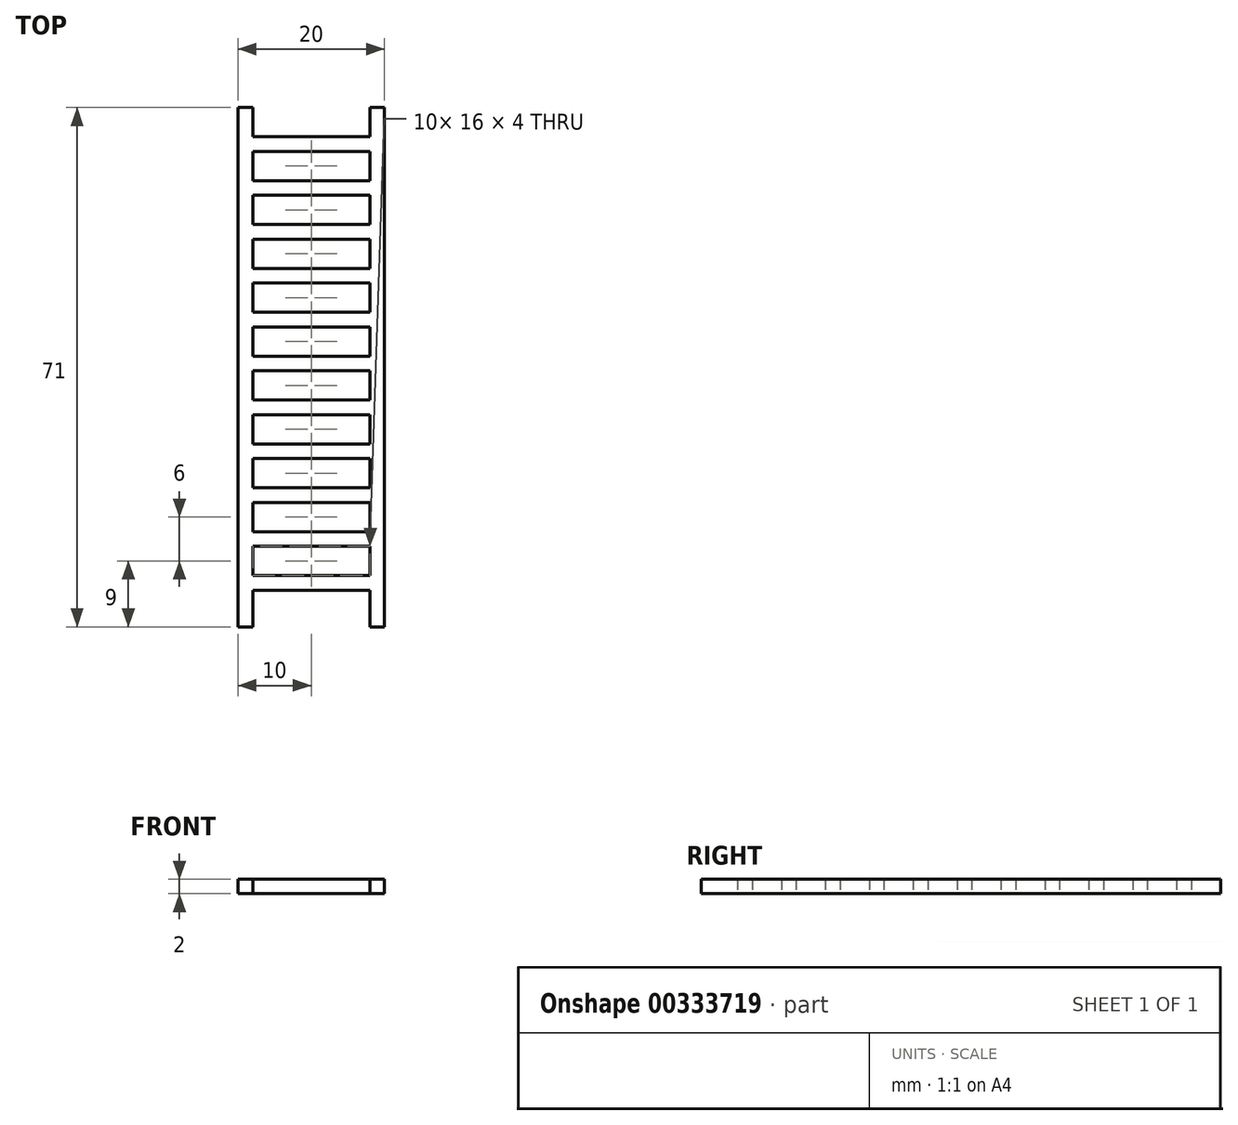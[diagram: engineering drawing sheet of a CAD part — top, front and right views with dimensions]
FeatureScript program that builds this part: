
annotation { "Feature Type Name" : "Feature", "Feature Type Description" : "" }
export const myFeature = defineFeature(function(context is Context, id is Id, definition is map)
    precondition{}
    {
        {
            var Q0;
            Q0=qCreatedBy(makeId("Top.planeOp"),FACE);
            var sketch = newSketch(context, id + "F0", { "sketchPlane" : qUnion([Q0])});
            skLineSegment(sketch, "E0.bottom", {"start": v(-10, 35.5) * mm, "end": v(10, 35.5) * mm, "construction": true});
            skLineSegment(sketch, "E0.top", {"start": v(-10, -35.5) * mm, "end": v(10, -35.5) * mm, "construction": true});
            skLineSegment(sketch, "E0.left", {"start": v(-10, 35.5) * mm, "end": v(-10, -35.5) * mm, "construction": true});
            skLineSegment(sketch, "E0.right", {"start": v(10, 35.5) * mm, "end": v(10, -35.5) * mm, "construction": true});
            skLineSegment(sketch, "E1", {"start": v(-10, 0) * mm, "end": v(10, 0) * mm, "construction": true});
            skLineSegment(sketch, "E2", {"start": v(0, 35.5) * mm, "end": v(0, -35.5) * mm, "construction": true});
            skLineSegment(sketch, "E3.bottom", {"start": v(-10, 35.5) * mm, "end": v(-8, 35.5) * mm});
            skLineSegment(sketch, "E3.top", {"start": v(-10, -35.5) * mm, "end": v(-8, -35.5) * mm});
            skLineSegment(sketch, "E3.left", {"start": v(-10, 35.5) * mm, "end": v(-10, -35.5) * mm});
            skLineSegment(sketch, "E3.right", {"start": v(-8, 35.5) * mm, "end": v(-8, -35.5) * mm});
            skLineSegment(sketch, "E4.bottom", {"start": v(10, -35.5) * mm, "end": v(8, -35.5) * mm});
            skLineSegment(sketch, "E4.top", {"start": v(10, 35.5) * mm, "end": v(8, 35.5) * mm});
            skLineSegment(sketch, "E4.left", {"start": v(10, -35.5) * mm, "end": v(10, 35.5) * mm});
            skLineSegment(sketch, "E4.right", {"start": v(8, -35.5) * mm, "end": v(8, 35.5) * mm});
            skLineSegment(sketch, "E5.bottom", {"start": v(-8, -28.5) * mm, "end": v(8, -28.5) * mm});
            skLineSegment(sketch, "E5.top", {"start": v(-8, -30.5) * mm, "end": v(8, -30.5) * mm});
            skLineSegment(sketch, "E5.left", {"start": v(-8, -28.5) * mm, "end": v(-8, -30.5) * mm});
            skLineSegment(sketch, "E5.right", {"start": v(8, -28.5) * mm, "end": v(8, -30.5) * mm});
            skLineSegment(sketch, "E6", {"start": v(-8, -29.5) * mm, "end": v(8, -29.5) * mm, "construction": true});
            skLineSegment(sketch, "E7.0.1.0", {"start": v(-8, -22.5) * mm, "end": v(8, -22.5) * mm});
            skLineSegment(sketch, "E7.0.1.1", {"start": v(-8, -24.5) * mm, "end": v(8, -24.5) * mm});
            skLineSegment(sketch, "E7.0.1.2", {"start": v(8, -22.5) * mm, "end": v(8, -24.5) * mm});
            skLineSegment(sketch, "E7.0.1.3", {"start": v(-8, -23.5) * mm, "end": v(8, -23.5) * mm, "construction": true});
            skLineSegment(sketch, "E7.0.1.4", {"start": v(-8, -22.5) * mm, "end": v(-8, -24.5) * mm});
            skLineSegment(sketch, "E7.0.2.0", {"start": v(-8, -16.5) * mm, "end": v(8, -16.5) * mm});
            skLineSegment(sketch, "E7.0.2.1", {"start": v(-8, -18.5) * mm, "end": v(8, -18.5) * mm});
            skLineSegment(sketch, "E7.0.2.2", {"start": v(8, -16.5) * mm, "end": v(8, -18.5) * mm});
            skLineSegment(sketch, "E7.0.2.3", {"start": v(-8, -17.5) * mm, "end": v(8, -17.5) * mm, "construction": true});
            skLineSegment(sketch, "E7.0.2.4", {"start": v(-8, -16.5) * mm, "end": v(-8, -18.5) * mm});
            skLineSegment(sketch, "E7.0.3.0", {"start": v(-8, -10.5) * mm, "end": v(8, -10.5) * mm});
            skLineSegment(sketch, "E7.0.3.1", {"start": v(-8, -12.5) * mm, "end": v(8, -12.5) * mm});
            skLineSegment(sketch, "E7.0.3.2", {"start": v(8, -10.5) * mm, "end": v(8, -12.5) * mm});
            skLineSegment(sketch, "E7.0.3.3", {"start": v(-8, -11.5) * mm, "end": v(8, -11.5) * mm, "construction": true});
            skLineSegment(sketch, "E7.0.3.4", {"start": v(-8, -10.5) * mm, "end": v(-8, -12.5) * mm});
            skLineSegment(sketch, "E7.0.4.0", {"start": v(-8, -4.5) * mm, "end": v(8, -4.5) * mm});
            skLineSegment(sketch, "E7.0.4.1", {"start": v(-8, -6.5) * mm, "end": v(8, -6.5) * mm});
            skLineSegment(sketch, "E7.0.4.2", {"start": v(8, -4.5) * mm, "end": v(8, -6.5) * mm});
            skLineSegment(sketch, "E7.0.4.3", {"start": v(-8, -5.5) * mm, "end": v(8, -5.5) * mm, "construction": true});
            skLineSegment(sketch, "E7.0.4.4", {"start": v(-8, -4.5) * mm, "end": v(-8, -6.5) * mm});
            skLineSegment(sketch, "E7.0.5.0", {"start": v(-8, 1.5) * mm, "end": v(8, 1.5) * mm});
            skLineSegment(sketch, "E7.0.5.1", {"start": v(-8, -0.5) * mm, "end": v(8, -0.5) * mm});
            skLineSegment(sketch, "E7.0.5.2", {"start": v(8, 1.5) * mm, "end": v(8, -0.5) * mm});
            skLineSegment(sketch, "E7.0.5.3", {"start": v(-8, 0.5) * mm, "end": v(8, 0.5) * mm, "construction": true});
            skLineSegment(sketch, "E7.0.5.4", {"start": v(-8, 1.5) * mm, "end": v(-8, -0.5) * mm});
            skLineSegment(sketch, "E7.0.6.0", {"start": v(-8, 7.5) * mm, "end": v(8, 7.5) * mm});
            skLineSegment(sketch, "E7.0.6.1", {"start": v(-8, 5.5) * mm, "end": v(8, 5.5) * mm});
            skLineSegment(sketch, "E7.0.6.2", {"start": v(8, 7.5) * mm, "end": v(8, 5.5) * mm});
            skLineSegment(sketch, "E7.0.6.3", {"start": v(-8, 6.5) * mm, "end": v(8, 6.5) * mm, "construction": true});
            skLineSegment(sketch, "E7.0.6.4", {"start": v(-8, 7.5) * mm, "end": v(-8, 5.5) * mm});
            skLineSegment(sketch, "E7.0.7.0", {"start": v(-8, 13.5) * mm, "end": v(8, 13.5) * mm});
            skLineSegment(sketch, "E7.0.7.1", {"start": v(-8, 11.5) * mm, "end": v(8, 11.5) * mm});
            skLineSegment(sketch, "E7.0.7.2", {"start": v(8, 13.5) * mm, "end": v(8, 11.5) * mm});
            skLineSegment(sketch, "E7.0.7.3", {"start": v(-8, 12.5) * mm, "end": v(8, 12.5) * mm, "construction": true});
            skLineSegment(sketch, "E7.0.7.4", {"start": v(-8, 13.5) * mm, "end": v(-8, 11.5) * mm});
            skLineSegment(sketch, "E7.0.8.0", {"start": v(-8, 19.5) * mm, "end": v(8, 19.5) * mm});
            skLineSegment(sketch, "E7.0.8.1", {"start": v(-8, 17.5) * mm, "end": v(8, 17.5) * mm});
            skLineSegment(sketch, "E7.0.8.2", {"start": v(8, 19.5) * mm, "end": v(8, 17.5) * mm});
            skLineSegment(sketch, "E7.0.8.3", {"start": v(-8, 18.5) * mm, "end": v(8, 18.5) * mm, "construction": true});
            skLineSegment(sketch, "E7.0.8.4", {"start": v(-8, 19.5) * mm, "end": v(-8, 17.5) * mm});
            skLineSegment(sketch, "E7.0.9.0", {"start": v(-8, 25.5) * mm, "end": v(8, 25.5) * mm});
            skLineSegment(sketch, "E7.0.9.1", {"start": v(-8, 23.5) * mm, "end": v(8, 23.5) * mm});
            skLineSegment(sketch, "E7.0.9.2", {"start": v(8, 25.5) * mm, "end": v(8, 23.5) * mm});
            skLineSegment(sketch, "E7.0.9.3", {"start": v(-8, 24.5) * mm, "end": v(8, 24.5) * mm, "construction": true});
            skLineSegment(sketch, "E7.0.9.4", {"start": v(-8, 25.5) * mm, "end": v(-8, 23.5) * mm});
            skLineSegment(sketch, "E7.0.10.0", {"start": v(-8, 31.5) * mm, "end": v(8, 31.5) * mm});
            skLineSegment(sketch, "E7.0.10.1", {"start": v(-8, 29.5) * mm, "end": v(8, 29.5) * mm});
            skLineSegment(sketch, "E7.0.10.2", {"start": v(8, 31.5) * mm, "end": v(8, 29.5) * mm});
            skLineSegment(sketch, "E7.0.10.3", {"start": v(-8, 30.5) * mm, "end": v(8, 30.5) * mm, "construction": true});
            skLineSegment(sketch, "E7.0.10.4", {"start": v(-8, 31.5) * mm, "end": v(-8, 29.5) * mm});
            skLineSegment(sketch, "E7.direction1", {"start": v(-8, -30.5) * mm, "end": v(17, -30.5) * mm, "construction": true});
            skLineSegment(sketch, "E7.direction2", {"start": v(-8, -30.5) * mm, "end": v(-8, -24.5) * mm, "construction": true});
            skSolve(sketch);
        }
        {
            var Q0;
            {var subQ11=sQuery(id+"F0.wireOp",EDGE,"E4.bottom");Q0=makeQuery(id+"F0.imprint","IMPRINT",FACE,{"disambiguationData":[TD([[makeQuery(id+"F0.imprint","IMPRINT",EDGE,{"derivedFrom":subQ11}),-1.0]])]});}
            var Q1;
            Q1=makeQuery(id+"F0.imprint","IMPRINT",FACE,{"disambiguationData":[TD([[makeQuery(id+"F0.imprint","IMPRINT",EDGE,{"derivedFrom":sQuery(id+"F0.wireOp",EDGE,"E5.bottom")}),-1.0]])]});
            var Q2;
            Q2=makeQuery(id+"F0.imprint","IMPRINT",FACE,{"disambiguationData":[TD([[makeQuery(id+"F0.imprint","IMPRINT",EDGE,{"derivedFrom":sQuery(id+"F0.wireOp",EDGE,"E7.0.1.0")}),-1.0]])]});
            var Q3;
            {var subQ9=sQuery(id+"F0.wireOp",EDGE,"E3.bottom");Q3=makeQuery(id+"F0.imprint","IMPRINT",FACE,{"disambiguationData":[TD([[makeQuery(id+"F0.imprint","IMPRINT",EDGE,{"derivedFrom":subQ9}),-1.0]])]});}
            var Q4;
            Q4=makeQuery(id+"F0.imprint","IMPRINT",FACE,{"disambiguationData":[TD([[makeQuery(id+"F0.imprint","IMPRINT",EDGE,{"derivedFrom":sQuery(id+"F0.wireOp",EDGE,"E7.0.2.0")}),-1.0]])]});
            var Q5;
            Q5=makeQuery(id+"F0.imprint","IMPRINT",FACE,{"disambiguationData":[TD([[makeQuery(id+"F0.imprint","IMPRINT",EDGE,{"derivedFrom":sQuery(id+"F0.wireOp",EDGE,"E7.0.3.0")}),-1.0]])]});
            var Q6;
            Q6=makeQuery(id+"F0.imprint","IMPRINT",FACE,{"disambiguationData":[TD([[makeQuery(id+"F0.imprint","IMPRINT",EDGE,{"derivedFrom":sQuery(id+"F0.wireOp",EDGE,"E7.0.4.0")}),-1.0]])]});
            var Q7;
            Q7=makeQuery(id+"F0.imprint","IMPRINT",FACE,{"disambiguationData":[TD([[makeQuery(id+"F0.imprint","IMPRINT",EDGE,{"derivedFrom":sQuery(id+"F0.wireOp",EDGE,"E7.0.5.0")}),-1.0]])]});
            var Q8;
            Q8=makeQuery(id+"F0.imprint","IMPRINT",FACE,{"disambiguationData":[TD([[makeQuery(id+"F0.imprint","IMPRINT",EDGE,{"derivedFrom":sQuery(id+"F0.wireOp",EDGE,"E7.0.6.0")}),-1.0]])]});
            var Q9;
            Q9=makeQuery(id+"F0.imprint","IMPRINT",FACE,{"disambiguationData":[TD([[makeQuery(id+"F0.imprint","IMPRINT",EDGE,{"derivedFrom":sQuery(id+"F0.wireOp",EDGE,"E7.0.7.0")}),-1.0]])]});
            var Q10;
            Q10=makeQuery(id+"F0.imprint","IMPRINT",FACE,{"disambiguationData":[TD([[makeQuery(id+"F0.imprint","IMPRINT",EDGE,{"derivedFrom":sQuery(id+"F0.wireOp",EDGE,"E7.0.8.0")}),-1.0]])]});
            var Q11;
            Q11=makeQuery(id+"F0.imprint","IMPRINT",FACE,{"disambiguationData":[TD([[makeQuery(id+"F0.imprint","IMPRINT",EDGE,{"derivedFrom":sQuery(id+"F0.wireOp",EDGE,"E7.0.10.0")}),-1.0]])]});
            var Q12;
            Q12=makeQuery(id+"F0.imprint","IMPRINT",FACE,{"disambiguationData":[TD([[makeQuery(id+"F0.imprint","IMPRINT",EDGE,{"derivedFrom":sQuery(id+"F0.wireOp",EDGE,"E7.0.9.0")}),-1.0]])]});
            extrude(context, id + "F1", {"entities" : qUnion([Q0, Q1, Q2, Q3, Q4, Q5, Q6, Q7, Q8, Q9, Q10, Q11, Q12]), "depth" : 2 * mm, "offsetDistance" : 25 * mm});
        }
    });
